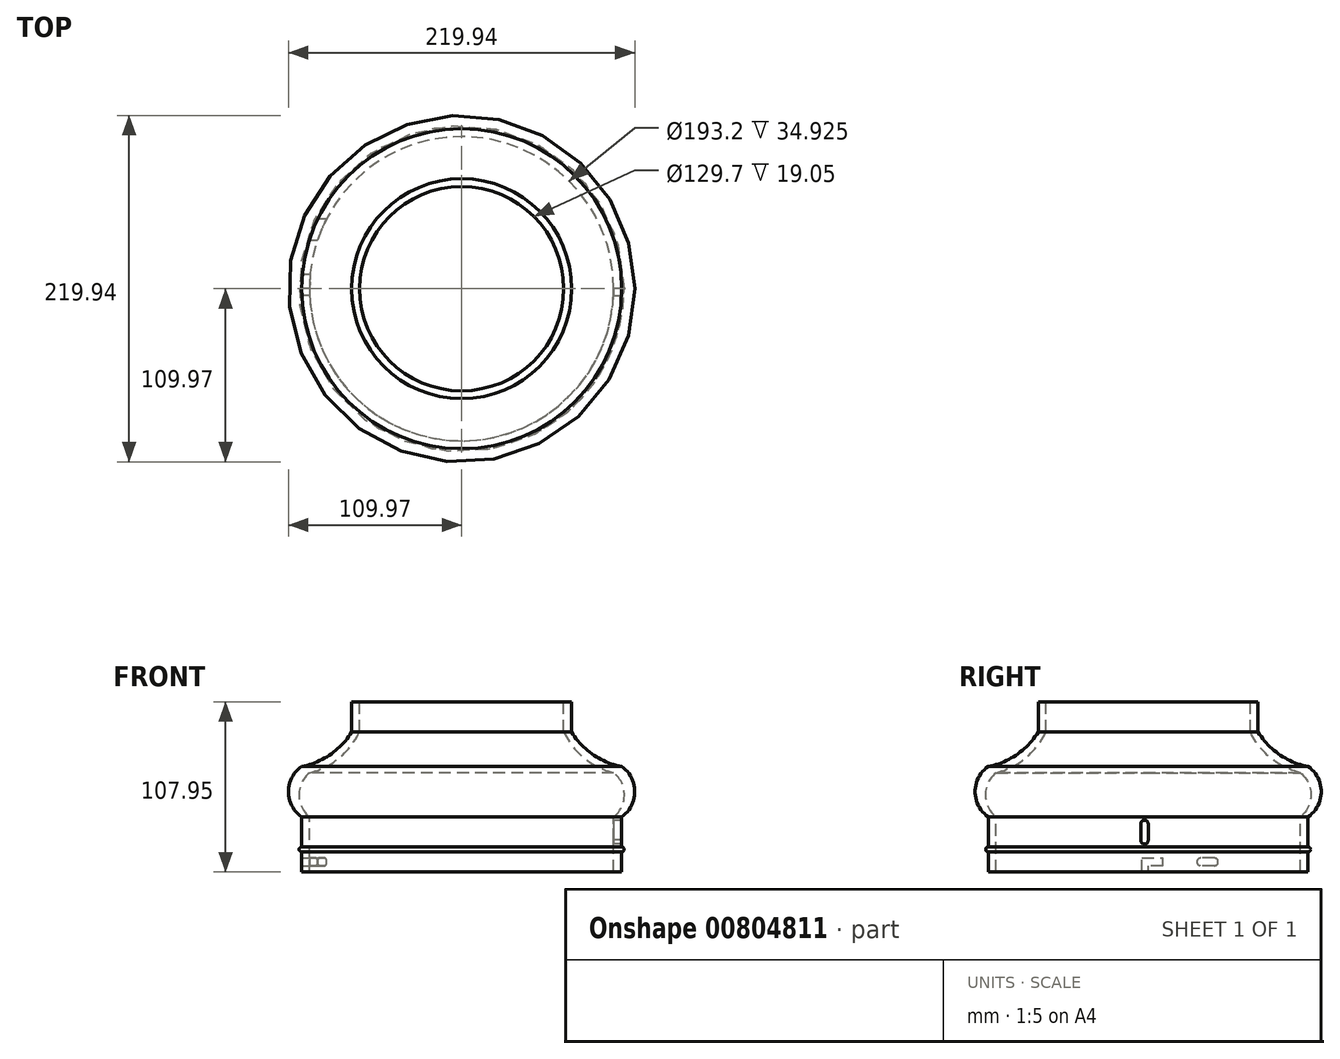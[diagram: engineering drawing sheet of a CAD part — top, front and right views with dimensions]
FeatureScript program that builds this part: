
annotation { "Feature Type Name" : "Feature", "Feature Type Description" : "" }
export const myFeature = defineFeature(function(context is Context, id is Id, definition is map)
    precondition{}
    {
        {
            var Q0;
            Q0=qCreatedBy(makeId("Front.planeOp"),FACE);
            var sketch = newSketch(context, id + "F0", { "sketchPlane" : qUnion([Q0])});
            skLineSegment(sketch, "E0.bottom", {"start": v(101.6, -107.95) * mm, "end": v(101.6, -107.95) * mm});
            skLineSegment(sketch, "E0.top", {"start": v(101.6, -95.25) * mm, "end": v(101.6, -95.25) * mm});
            skLineSegment(sketch, "E0.left", {"start": v(101.6, -107.95) * mm, "end": v(101.6, -95.25) * mm});
            skLineSegment(sketch, "E0.right", {"start": v(101.6, -107.95) * mm, "end": v(101.6, -95.25) * mm});
            skArc(sketch, "E1", {"start": v(101.6, -95.25) * mm, "mid": v(103.19, -93.66) * mm, "end": v(101.6, -92.08) * mm});
            skLineSegment(sketch, "E2", {"start": v(101.6, -92.08) * mm, "end": v(101.6, -73.03) * mm});
            skLineSegment(sketch, "E3", {"start": v(69.85, 0) * mm, "end": v(69.85, -19.05) * mm});
            skArc(sketch, "E4", {"start": v(101.6, -73.03) * mm, "mid": v(109.97, -56.99) * mm, "end": v(101.6, -40.95) * mm});
            skArc(sketch, "E5", {"start": v(69.85, -19.05) * mm, "mid": v(83.39, -33.4) * mm, "end": v(101.6, -40.95) * mm});
            skLineSegment(sketch, "E6", {"start": v(69.85, 0) * mm, "end": v(64.85, 0) * mm});
            skLineSegment(sketch, "E7", {"start": v(64.85, 0) * mm, "end": v(64.85, -19.05) * mm});
            skLineSegment(sketch, "E8", {"start": v(101.6, -107.95) * mm, "end": v(96.6, -107.95) * mm});
            skLineSegment(sketch, "E9", {"start": v(96.6, -107.95) * mm, "end": v(96.6, -73.03) * mm});
            skPoint(sketch, "E10", {"position": v(96.6, -44.94) * mm});
            skArc(sketch, "E11", {"start": v(64.85, -19.05) * mm, "mid": v(77.78, -35.6) * mm, "end": v(96.6, -44.94) * mm});
            skArc(sketch, "E12", {"start": v(96.6, -73.03) * mm, "mid": v(103.36, -58.98) * mm, "end": v(96.6, -44.94) * mm});
            skSolve(sketch);
        }
        {
            var Q0;
            Q0=qCreatedBy(makeId("Front.planeOp"),FACE);
            var sketch = newSketch(context, id + "F1", { "sketchPlane" : qUnion([Q0])});
            skLineSegment(sketch, "E13", {"start": v(0, -1.96) * mm, "end": v(0, -72.7) * mm});
            skSolve(sketch);
        }
        {
            var Q0;
            Q0=qSketchRegion(id+"F0",true);
            var Q1;
            Q1=sQuery(id+"F1.wireOp",EDGE,"E13");
            revolve(context, id + "F2", {"entities" : qUnion([Q0]), "axis" : qUnion([Q1]), "revolveType" : RevolveType.FULL});
        }
        {
            var Q0;
            Q0=qCreatedBy(makeId("Right.planeOp"),FACE);
            var sketch = newSketch(context, id + "F3", { "sketchPlane" : qUnion([Q0])});
            skLineSegment(sketch, "E14", {"start": v(0, -77.44) * mm, "end": v(0, -87.66) * mm});
            skLineSegment(sketch, "E15", {"start": v(0, -77.44) * mm, "end": v(-4.73, -77.44) * mm});
            skLineSegment(sketch, "E16", {"start": v(-4.73, -87.89) * mm, "end": v(0, -87.66) * mm});
            skLineSegment(sketch, "E17", {"start": v(-4.73, -77.44) * mm, "end": v(-4.73, -87.89) * mm});
            skArc(sketch, "E18", {"start": v(-4.73, -87.89) * mm, "mid": v(-2.25, -90.25) * mm, "end": v(0, -87.66) * mm});
            skArc(sketch, "E19", {"start": v(0, -77.44) * mm, "mid": v(-2.36, -75.07) * mm, "end": v(-4.73, -77.44) * mm});
            skSolve(sketch);
        }
        {
            var Q0;
            Q0=qSketchRegion(id+"F3",true);
            extrude(context, id + "F4", {"entities" : qUnion([Q0]), "operationType" : NewBodyOperationType.REMOVE, "depth" : 2540 * mm});
        }
        {
            var Q0;
            Q0=qCreatedBy(makeId("Right.planeOp"),FACE);
            var sketch = newSketch(context, id + "F5", { "sketchPlane" : qUnion([Q0])});
            skLineSegment(sketch, "E20.bottom", {"start": v(42.01, -99.17) * mm, "end": v(33.4, -99.17) * mm});
            skLineSegment(sketch, "E20.top", {"start": v(42.01, -104.03) * mm, "end": v(33.4, -104.03) * mm});
            skLineSegment(sketch, "E20.left", {"start": v(42.01, -99.17) * mm, "end": v(42.01, -104.03) * mm});
            skLineSegment(sketch, "E20.right", {"start": v(33.4, -99.17) * mm, "end": v(33.4, -104.03) * mm});
            skArc(sketch, "E21", {"start": v(33.4, -99.17) * mm, "mid": v(30.96, -101.6) * mm, "end": v(33.4, -104.03) * mm});
            skArc(sketch, "E22", {"start": v(42.01, -104.03) * mm, "mid": v(44.45, -101.6) * mm, "end": v(42.01, -99.17) * mm});
            skLineSegment(sketch, "E23.bottom", {"start": v(0, -107.97) * mm, "end": v(0, -107.97) * mm});
            skLineSegment(sketch, "E24.bottom", {"start": v(0, -106.15) * mm, "end": v(0, -106.15) * mm});
            skLineSegment(sketch, "E25.bottom", {"start": v(-2.16, -103.35) * mm, "end": v(-1.97, -103.35) * mm});
            skLineSegment(sketch, "E25.top", {"start": v(-2.16, -107.95) * mm, "end": v(-1.97, -107.95) * mm});
            skLineSegment(sketch, "E26", {"start": v(-1.97, -99.17) * mm, "end": v(9.35, -99.17) * mm});
            skLineSegment(sketch, "E27", {"start": v(9.35, -99.17) * mm, "end": v(9.35, -103.35) * mm});
            skLineSegment(sketch, "E28", {"start": v(9.35, -99.17) * mm, "end": v(9.35, -104.03) * mm});
            skLineSegment(sketch, "E29", {"start": v(-1.97, -99.17) * mm, "end": v(-3.88, -99.17) * mm});
            skLineSegment(sketch, "E30", {"start": v(-3.88, -99.17) * mm, "end": v(-3.88, -107.95) * mm});
            skLineSegment(sketch, "E31", {"start": v(9.35, -104.03) * mm, "end": v(0, -104.03) * mm});
            skLineSegment(sketch, "E32", {"start": v(0, -104.03) * mm, "end": v(0, -107.97) * mm});
            skLineSegment(sketch, "E33", {"start": v(0, -107.97) * mm, "end": v(-3.88, -107.95) * mm});
            skSolve(sketch);
        }
        {
            var Q0;
            Q0=qSketchRegion(id+"F5",true);
            extrude(context, id + "F6", {"entities" : qUnion([Q0]), "operationType" : NewBodyOperationType.REMOVE, "oppositeDirection" : true, "depth" : 2540 * mm});
        }
    });
